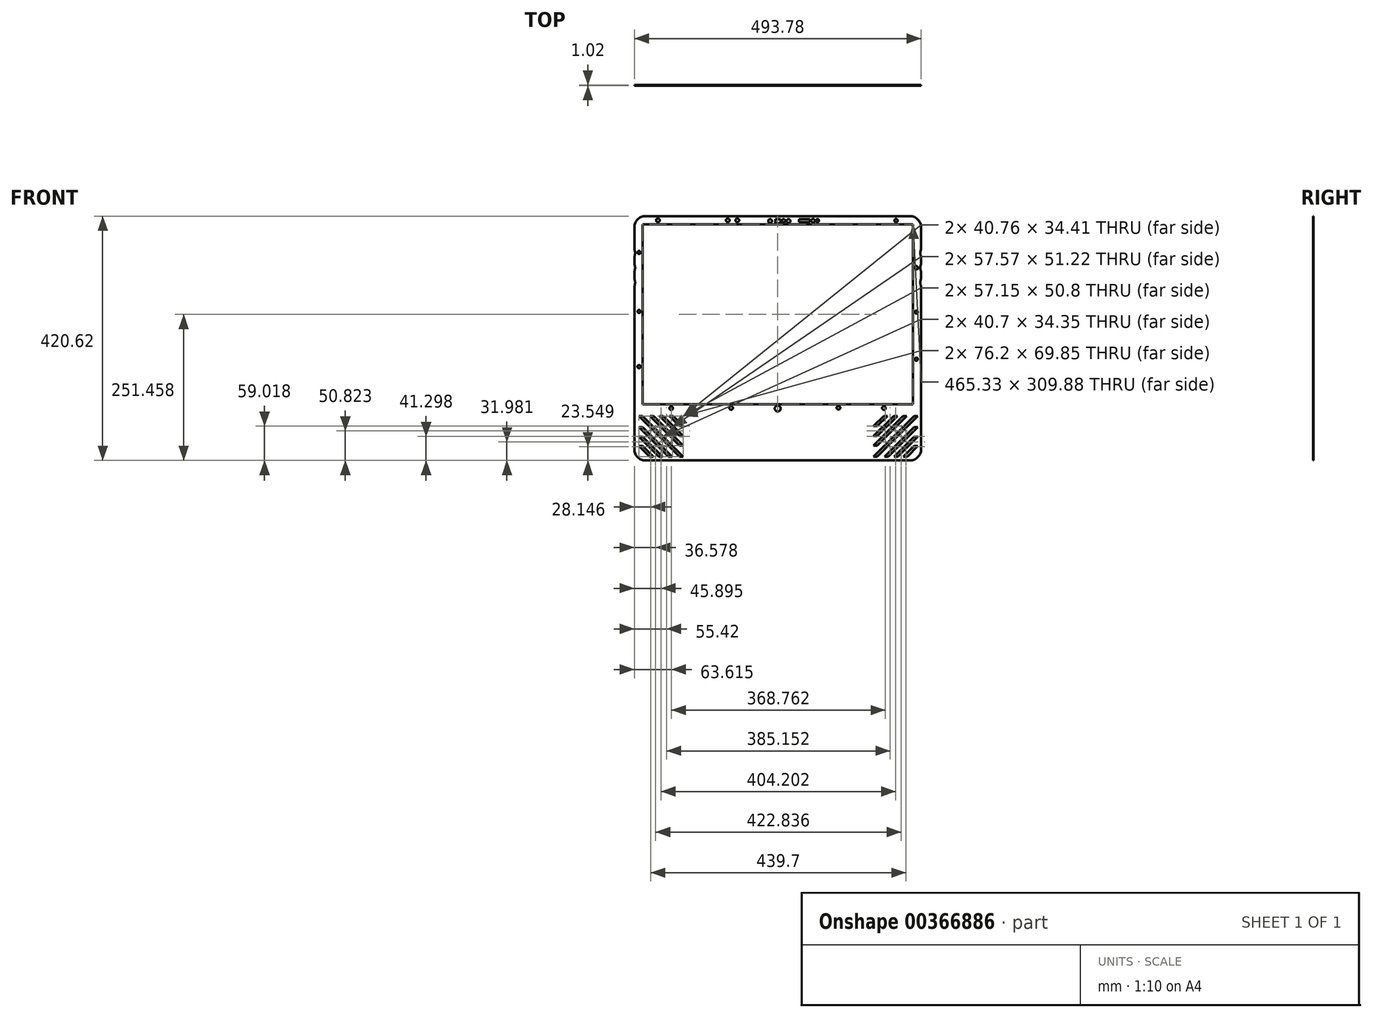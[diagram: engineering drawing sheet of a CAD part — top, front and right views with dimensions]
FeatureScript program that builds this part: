
annotation { "Feature Type Name" : "Feature", "Feature Type Description" : "" }
export const myFeature = defineFeature(function(context is Context, id is Id, definition is map)
    precondition{}
    {
        {
            var Q0;
            Q0=qCreatedBy(makeId("Front.planeOp"),FACE);
            var sketch = newSketch(context, id + "F0", { "sketchPlane" : qUnion([Q0])});
            skLineSegment(sketch, "E0.bottom", {"start": v(227.84, 210.31) * mm, "end": v(-227.84, 210.31) * mm});
            skLineSegment(sketch, "E0.top", {"start": v(227.84, -210.31) * mm, "end": v(-227.84, -210.31) * mm});
            skLineSegment(sketch, "E0.left", {"start": v(246.89, 191.26) * mm, "end": v(246.89, -191.26) * mm});
            skLineSegment(sketch, "E0.right", {"start": v(-246.89, 191.26) * mm, "end": v(-246.89, -191.26) * mm});
            skPoint(sketch, "E0.middle", {"position": v(0, 0) * mm});
            skPoint(sketch, "E1.visualSharp", {"position": v(-246.89, 210.31) * mm});
            skArc(sketch, "E1.filletArc", {"start": v(-227.84, 210.31) * mm, "mid": v(-241.3, 204.73) * mm, "end": v(-246.89, 191.26) * mm});
            skPoint(sketch, "E2.visualSharp", {"position": v(246.89, 210.31) * mm});
            skArc(sketch, "E2.filletArc", {"start": v(246.89, 191.26) * mm, "mid": v(241.3, 204.73) * mm, "end": v(227.84, 210.31) * mm});
            skPoint(sketch, "E3.visualSharp", {"position": v(246.89, -210.31) * mm});
            skArc(sketch, "E3.filletArc", {"start": v(227.84, -210.31) * mm, "mid": v(241.3, -204.73) * mm, "end": v(246.89, -191.26) * mm});
            skPoint(sketch, "E4.visualSharp", {"position": v(-246.89, -210.31) * mm});
            skArc(sketch, "E4.filletArc", {"start": v(-246.89, -191.26) * mm, "mid": v(-241.3, -204.73) * mm, "end": v(-227.84, -210.31) * mm});
            skSolve(sketch);
        }
        {
            var Q0;
            Q0=qCreatedBy(makeId("Front.planeOp"),FACE);
            var sketch = newSketch(context, id + "F1", { "sketchPlane" : qUnion([Q0])});
            skLineSegment(sketch, "E5.bottom", {"start": v(-232.66, 196.09) * mm, "end": v(232.66, 196.09) * mm});
            skLineSegment(sketch, "E5.top", {"start": v(-232.66, -113.8) * mm, "end": v(232.66, -113.8) * mm});
            skLineSegment(sketch, "E5.left", {"start": v(-232.66, 196.09) * mm, "end": v(-232.66, -113.8) * mm});
            skLineSegment(sketch, "E5.right", {"start": v(232.66, 196.09) * mm, "end": v(232.66, -113.8) * mm});
            skSolve(sketch);
        }
        {
            var Q0;
            Q0 = qSketchRegion(id + "F0", true);
            extrude(context, id + "F2", {"entities" : qUnion([Q0]), "depth" : 1.02 * mm});
        }
        {
            var Q0;
            Q0 = qSketchRegion(id + "F1", true);
            extrude(context, id + "F3", {"entities" : qUnion([Q0]), "operationType" : NewBodyOperationType.REMOVE, "depth" : 2.54 * mm});
        }
        {
            var Q0;
            Q0=qCreatedBy(makeId("Front.planeOp"),FACE);
            var sketch = newSketch(context, id + "F4", { "sketchPlane" : qUnion([Q0])});
            skLineSegment(sketch, "E6.bottom", {"start": v(-4.06, 205.23) * mm, "end": v(5.08, 205.23) * mm});
            skLineSegment(sketch, "E6.top", {"start": v(-4.06, 198.12) * mm, "end": v(5.08, 198.12) * mm});
            skLineSegment(sketch, "E6.left", {"start": v(-4.06, 205.23) * mm, "end": v(-4.06, 198.12) * mm});
            skLineSegment(sketch, "E6.right", {"start": v(5.08, 205.23) * mm, "end": v(5.08, 198.12) * mm});
            skCircle(sketch, "E7", {"center": v(-13.08, 201.97) * mm, "radius": 3.24 * mm});
            skCircle(sketch, "E8", {"center": v(9.97, 202.25) * mm, "radius": 2.93 * mm});
            skCircle(sketch, "E9", {"center": v(18.5, 201.97) * mm, "radius": 3.27 * mm});
            skLineSegment(sketch, "E10.bottom", {"start": v(36.83, 205.23) * mm, "end": v(55.88, 205.23) * mm});
            skLineSegment(sketch, "E10.top", {"start": v(36.83, 200.15) * mm, "end": v(55.88, 200.15) * mm});
            skLineSegment(sketch, "E10.left", {"start": v(36.83, 205.23) * mm, "end": v(36.83, 200.15) * mm});
            skLineSegment(sketch, "E10.right", {"start": v(55.88, 205.23) * mm, "end": v(55.88, 200.15) * mm});
            skCircle(sketch, "E11", {"center": v(68.58, 202.7) * mm, "radius": 2.56 * mm});
            skCircle(sketch, "E12", {"center": v(203.7, 202.7) * mm, "radius": 2.82 * mm});
            skCircle(sketch, "E13", {"center": v(0, -120.9) * mm, "radius": 5.08 * mm});
            skSolve(sketch);
        }
        {
            var Q0;
            Q0 = qSketchRegion(id + "F4", true);
            extrude(context, id + "F5", {"entities" : qUnion([Q0]), "operationType" : NewBodyOperationType.REMOVE, "depth" : 25.4 * mm});
        }
        {
            var Q0;
            Q0=qCreatedBy(makeId("Front.planeOp"),FACE);
            var sketch = newSketch(context, id + "F6", { "sketchPlane" : qUnion([Q0])});
            skCircle(sketch, "E14", {"center": v(60.96, 202.38) * mm, "radius": 3.18 * mm});
            skCircle(sketch, "E15", {"center": v(-69.58, 203.2) * mm, "radius": 3.18 * mm});
            skCircle(sketch, "E16", {"center": v(-85.96, 203.2) * mm, "radius": 3.18 * mm});
            skCircle(sketch, "E17", {"center": v(-206.25, 203.2) * mm, "radius": 3.18 * mm});
            skCircle(sketch, "E18", {"center": v(104.65, -119.62) * mm, "radius": 3.09 * mm});
            skSolve(sketch);
        }
        {
            var Q0;
            Q0 = qSketchRegion(id + "F6", true);
            extrude(context, id + "F7", {"entities" : qUnion([Q0]), "operationType" : NewBodyOperationType.REMOVE, "depth" : 25.4 * mm});
        }
        {
            var Q0;
            Q0=qCreatedBy(makeId("Front.planeOp"),FACE);
            var sketch = newSketch(context, id + "F8", { "sketchPlane" : qUnion([Q0])});
            skCircle(sketch, "E19", {"center": v(-183.39, -120.36) * mm, "radius": 3.01 * mm});
            skCircle(sketch, "E20", {"center": v(-80.26, -119.84) * mm, "radius": 3.15 * mm});
            skCircle(sketch, "E21", {"center": v(182.88, -120.14) * mm, "radius": 3.12 * mm});
            skCircle(sketch, "E22", {"center": v(-238.76, 147.83) * mm, "radius": 2.56 * mm});
            skCircle(sketch, "E23", {"center": v(-238.76, 46.23) * mm, "radius": 2.56 * mm});
            skCircle(sketch, "E24", {"center": v(-238.76, -48.77) * mm, "radius": 2.76 * mm});
            skCircle(sketch, "E25", {"center": v(238.76, 121.41) * mm, "radius": 2.77 * mm});
            skCircle(sketch, "E26", {"center": v(238.76, 45.21) * mm, "radius": 2.57 * mm});
            skCircle(sketch, "E27", {"center": v(238.76, -36.07) * mm, "radius": 2.63 * mm});
            skSolve(sketch);
        }
        {
            var Q0;
            Q0 = qSketchRegion(id + "F8", true);
            extrude(context, id + "F9", {"entities" : qUnion([Q0]), "operationType" : NewBodyOperationType.REMOVE, "depth" : 25.4 * mm});
        }
        {
            var Q0;
            Q0=qCreatedBy(makeId("Front.planeOp"),FACE);
            var sketch = newSketch(context, id + "F10", { "sketchPlane" : qUnion([Q0])});
            skLineSegment(sketch, "E28", {"start": v(-239.1, -134.09) * mm, "end": v(-232.74, -134.09) * mm});
            skLineSegment(sketch, "E29", {"start": v(-232.74, -134.09) * mm, "end": v(-162.9, -203.94) * mm});
            skLineSegment(sketch, "E30", {"start": v(-162.9, -203.94) * mm, "end": v(-169.24, -203.94) * mm});
            skLineSegment(sketch, "E31", {"start": v(-169.24, -203.94) * mm, "end": v(-239.1, -134.09) * mm});
            skLineSegment(sketch, "E32", {"start": v(-220.04, -134.09) * mm, "end": v(-213.7, -134.09) * mm});
            skPoint(sketch, "E33.endSnap0", {"position": v(-166.07, -203.94) * mm});
            skLineSegment(sketch, "E34", {"start": v(-162.9, -184.89) * mm, "end": v(-169.24, -184.89) * mm});
            skLineSegment(sketch, "E35", {"start": v(-169.24, -184.89) * mm, "end": v(-220.04, -134.09) * mm});
            skLineSegment(sketch, "E36", {"start": v(-213.7, -134.09) * mm, "end": v(-162.9, -184.89) * mm});
            skLineSegment(sketch, "E37", {"start": v(-239.1, -152.72) * mm, "end": v(-232.74, -152.72) * mm});
            skLineSegment(sketch, "E38", {"start": v(-232.74, -152.72) * mm, "end": v(-181.53, -203.94) * mm});
            skLineSegment(sketch, "E39", {"start": v(-181.53, -203.94) * mm, "end": v(-187.88, -203.94) * mm});
            skLineSegment(sketch, "E40", {"start": v(-187.88, -203.94) * mm, "end": v(-239.1, -152.72) * mm});
            skLineSegment(sketch, "E41", {"start": v(-239.1, -169.59) * mm, "end": v(-232.74, -169.59) * mm});
            skLineSegment(sketch, "E42", {"start": v(-232.74, -169.59) * mm, "end": v(-198.4, -203.94) * mm});
            skLineSegment(sketch, "E43", {"start": v(-198.4, -203.94) * mm, "end": v(-204.74, -203.94) * mm});
            skLineSegment(sketch, "E44", {"start": v(-204.74, -203.94) * mm, "end": v(-239.1, -169.59) * mm});
            skLineSegment(sketch, "E45", {"start": v(-239.1, -185.63) * mm, "end": v(-232.74, -185.63) * mm});
            skLineSegment(sketch, "E46", {"start": v(-232.74, -185.63) * mm, "end": v(-214.44, -203.94) * mm});
            skLineSegment(sketch, "E47", {"start": v(-214.44, -203.94) * mm, "end": v(-220.8, -203.94) * mm});
            skLineSegment(sketch, "E48", {"start": v(-220.8, -203.94) * mm, "end": v(-239.1, -185.63) * mm});
            skLineSegment(sketch, "E49", {"start": v(-162.9, -168.5) * mm, "end": v(-169.24, -168.5) * mm});
            skLineSegment(sketch, "E50", {"start": v(-169.24, -168.5) * mm, "end": v(-203.65, -134.09) * mm});
            skLineSegment(sketch, "E51", {"start": v(-203.65, -134.09) * mm, "end": v(-197.3, -134.09) * mm});
            skLineSegment(sketch, "E52", {"start": v(-197.3, -134.09) * mm, "end": v(-162.9, -168.5) * mm});
            skLineSegment(sketch, "E53", {"start": v(-162.9, -151.36) * mm, "end": v(-169.24, -151.36) * mm});
            skLineSegment(sketch, "E54", {"start": v(-169.24, -151.36) * mm, "end": v(-186.52, -134.09) * mm});
            skLineSegment(sketch, "E55", {"start": v(-186.52, -134.09) * mm, "end": v(-180.17, -134.09) * mm});
            skLineSegment(sketch, "E56", {"start": v(-180.17, -134.09) * mm, "end": v(-162.9, -151.36) * mm});
            skLineSegment(sketch, "E57.MirrorCS", {"start": v(171.46, -203.94) * mm, "end": v(241.3, -134.09) * mm});
            skLineSegment(sketch, "E58.MirrorCS", {"start": v(223, -203.94) * mm, "end": v(241.3, -185.63) * mm});
            skLineSegment(sketch, "E59.MirrorCS", {"start": v(234.96, -185.63) * mm, "end": v(216.65, -203.94) * mm});
            skLineSegment(sketch, "E60.MirrorCS", {"start": v(206.96, -203.94) * mm, "end": v(241.3, -169.59) * mm});
            skLineSegment(sketch, "E61.MirrorCS", {"start": v(234.96, -169.59) * mm, "end": v(200.6, -203.94) * mm});
            skLineSegment(sketch, "E62.MirrorCS", {"start": v(190.1, -203.94) * mm, "end": v(241.3, -152.72) * mm});
            skLineSegment(sketch, "E63.MirrorCS", {"start": v(234.96, -152.72) * mm, "end": v(183.74, -203.94) * mm});
            skLineSegment(sketch, "E64.MirrorCS", {"start": v(234.96, -134.09) * mm, "end": v(165.1, -203.94) * mm});
            skLineSegment(sketch, "E65.MirrorCS", {"start": v(171.46, -184.89) * mm, "end": v(222.26, -134.09) * mm});
            skLineSegment(sketch, "E66.MirrorCS", {"start": v(171.46, -168.5) * mm, "end": v(205.87, -134.09) * mm});
            skLineSegment(sketch, "E67.MirrorCS", {"start": v(171.46, -151.36) * mm, "end": v(188.73, -134.09) * mm});
            skLineSegment(sketch, "E68.MirrorCS", {"start": v(182.38, -134.09) * mm, "end": v(165.1, -151.36) * mm});
            skLineSegment(sketch, "E69.MirrorCS", {"start": v(188.73, -134.09) * mm, "end": v(182.38, -134.09) * mm});
            skLineSegment(sketch, "E70.MirrorCS", {"start": v(205.87, -134.09) * mm, "end": v(199.52, -134.09) * mm});
            skLineSegment(sketch, "E71.MirrorCS", {"start": v(222.26, -134.09) * mm, "end": v(215.9, -134.09) * mm});
            skLineSegment(sketch, "E72.MirrorCS", {"start": v(241.3, -134.09) * mm, "end": v(234.96, -134.09) * mm});
            skLineSegment(sketch, "E73.MirrorCS", {"start": v(241.3, -152.72) * mm, "end": v(234.96, -152.72) * mm});
            skLineSegment(sketch, "E74.MirrorCS", {"start": v(241.3, -169.59) * mm, "end": v(234.96, -169.59) * mm});
            skLineSegment(sketch, "E75.MirrorCS", {"start": v(241.3, -185.63) * mm, "end": v(234.96, -185.63) * mm});
            skLineSegment(sketch, "E76.MirrorCS", {"start": v(216.65, -203.94) * mm, "end": v(223, -203.94) * mm});
            skLineSegment(sketch, "E77.MirrorCS", {"start": v(200.6, -203.94) * mm, "end": v(206.96, -203.94) * mm});
            skLineSegment(sketch, "E78.MirrorCS", {"start": v(183.74, -203.94) * mm, "end": v(190.1, -203.94) * mm});
            skPoint(sketch, "E79.MirrorP", {"position": v(168.28, -203.94) * mm});
            skLineSegment(sketch, "E80.MirrorCS", {"start": v(165.1, -184.89) * mm, "end": v(171.46, -184.89) * mm});
            skLineSegment(sketch, "E81.MirrorCS", {"start": v(165.1, -168.5) * mm, "end": v(171.46, -168.5) * mm});
            skLineSegment(sketch, "E82.MirrorCS", {"start": v(165.1, -151.36) * mm, "end": v(171.46, -151.36) * mm});
            skLineSegment(sketch, "E83.MirrorCS", {"start": v(199.52, -134.09) * mm, "end": v(165.1, -168.5) * mm});
            skLineSegment(sketch, "E84.MirrorCS", {"start": v(215.9, -134.09) * mm, "end": v(165.1, -184.89) * mm});
            skLineSegment(sketch, "E85", {"start": v(165.1, -203.94) * mm, "end": v(171.46, -203.94) * mm});
            skSolve(sketch);
        }
        {
            var Q0;
            Q0 = qSketchRegion(id + "F10", true);
            extrude(context, id + "F11", {"entities" : qUnion([Q0]), "operationType" : NewBodyOperationType.REMOVE, "depth" : 25.4 * mm});
        }
        {
            var Q0;
            Q0=qCreatedBy(makeId("Front.planeOp"),FACE);
            var sketch = newSketch(context, id + "F12", { "sketchPlane" : qUnion([Q0])});
            skCircle(sketch, "E86", {"center": v(-264.67, 146.81) * mm, "radius": 19.05 * mm});
            skCircle(sketch, "E87", {"center": v(-264.67, 121.41) * mm, "radius": 19.05 * mm});
            skCircle(sketch, "E88", {"center": v(-264.67, 96.01) * mm, "radius": 19.05 * mm});
            skCircle(sketch, "E89", {"center": v(264.67, 146.81) * mm, "radius": 19.05 * mm});
            skCircle(sketch, "E90", {"center": v(264.67, 121.41) * mm, "radius": 19.05 * mm});
            skCircle(sketch, "E91", {"center": v(264.67, 96.01) * mm, "radius": 19.05 * mm});
            skSolve(sketch);
        }
        {
            var Q0;
            Q0 = qSketchRegion(id + "F12", true);
            extrude(context, id + "F13", {"entities" : qUnion([Q0]), "operationType" : NewBodyOperationType.REMOVE, "depth" : 25.4 * mm});
        }
    });
